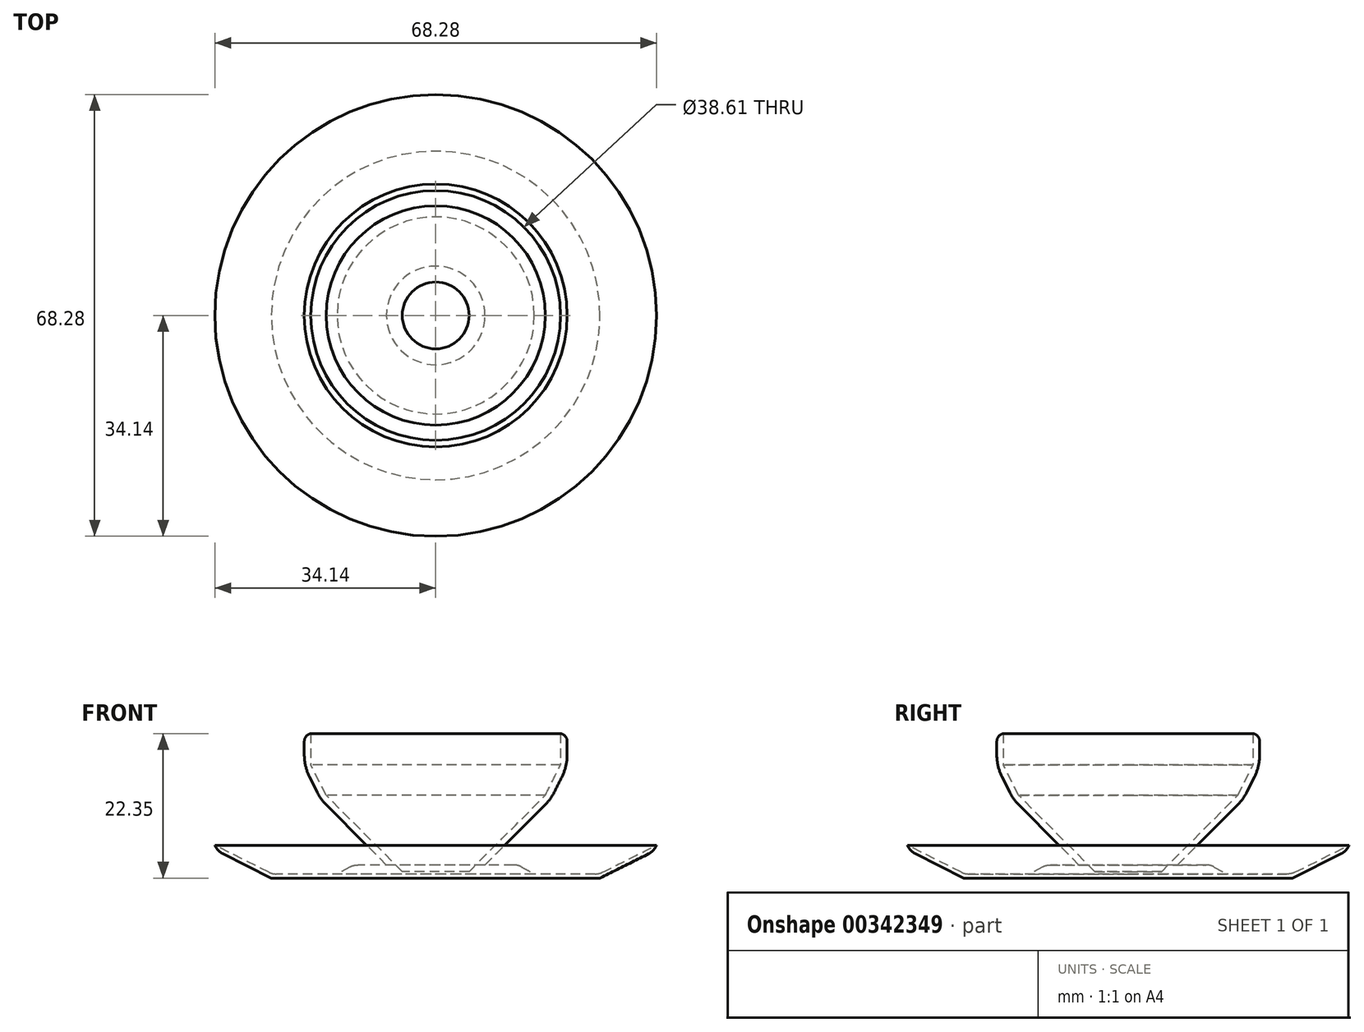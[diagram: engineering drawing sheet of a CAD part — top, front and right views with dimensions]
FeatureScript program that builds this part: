
annotation { "Feature Type Name" : "Feature", "Feature Type Description" : "" }
export const myFeature = defineFeature(function(context is Context, id is Id, definition is map)
    precondition{}
    {
        {
            var Q0;
            Q0=qCreatedBy(makeId("Top.planeOp"),FACE);
            var sketch = newSketch(context, id + "F0", { "sketchPlane" : qUnion([Q0])});
            skCircle(sketch, "E0", {"center": v(0, 0) * mm, "radius": 25.4 * mm});
            skSolve(sketch);
        }
        {
            var Q0;
            Q0=qCreatedBy(makeId("Top.planeOp"),FACE);
            cPlane(context, id + "F1", {"entities" : qUnion([Q0]), "cplaneType" : CPlaneType.OFFSET, "offset" : 5.08 * mm, "width" : 152.4 * mm, "height" : 152.4 * mm});
        }
        {
            var Q0;
            Q0=qCreatedBy(id+"F1.planeOp",FACE);
            var sketch = newSketch(context, id + "F2", { "sketchPlane" : qUnion([Q0])});
            skCircle(sketch, "E1", {"center": v(0, 0) * mm, "radius": 35.56 * mm});
            skSolve(sketch);
        }
        {
            var Q0;
            Q0 = qSketchRegion(id + "F0", true);
            var Q1;
            Q1=makeQuery(id+"F2.imprint","IMPRINT",FACE,{"disambiguationData":[TD([[makeQuery(id+"F2.imprint","IMPRINT",EDGE,{"derivedFrom":sQuery(id+"F2.wireOp",EDGE,"E1")}),1.0]])]});
            loft(context, id + "F3", {"sheetProfilesArray" : [{ "sheetProfileEntities" : qUnion([Q0]) }, { "sheetProfileEntities" : qUnion([Q1]) }]});
        }
        {
            var Q0;
            Q0=makeQuery(id+"F3.opLoft","CAP_FACE",FACE,{"disambiguationData":[OSD([makeQuery(id+"F2.imprint","IMPRINT",FACE,{"disambiguationData":[TD([[makeQuery(id+"F2.imprint","IMPRINT",EDGE,{"derivedFrom":sQuery(id+"F2.wireOp",EDGE,"E1")}),1.0]])]})])],"isStart":true});
            shell(context, id + "F4", {"entities" : qUnion([Q0]), "thickness" : 0.64 * mm});
        }
        {
            var Q0;
            Q0=qCreatedBy(makeId("Top.planeOp"),FACE);
            var Q1;
            Q1 = qBodyType(qCreatedBy(id + "FbNprcCNBa9596W_1" ,EDGE), BodyType.WIRE);
            cPlane(context, id + "F5", {"entities" : qUnion([Q0, Q1]), "cplaneType" : CPlaneType.OFFSET, "offset" : 2.03 * mm, "width" : 152.4 * mm, "height" : 152.4 * mm});
        }
        {
            var Q0;
            Q0=qCreatedBy(id+"F5.planeOp",FACE);
            var sketch = newSketch(context, id + "F6", { "sketchPlane" : qUnion([Q0])});
            skCircle(sketch, "E2", {"center": v(0, 0) * mm, "radius": 12.7 * mm});
            skSolve(sketch);
        }
        {
            var Q0;
            Q0=makeQuery(id+"F4.opShell","OFFSET_FACE",FACE,{"disambiguationData":[OSD([makeQuery(id+"F0.imprint","IMPRINT",FACE,{"disambiguationData":[TD([[makeQuery(id+"F0.imprint","IMPRINT",EDGE,{"derivedFrom":sQuery(id+"F0.wireOp",EDGE,"E0")}),1.0]])]})])]});
            var sketch = newSketch(context, id + "F7", { "sketchPlane" : qUnion([Q0])});
            skCircle(sketch, "E3", {"center": v(0, 0) * mm, "radius": 15.24 * mm});
            skSolve(sketch);
        }
        {
            var Q1;
            Q1=makeQuery(id+"F7.imprint","IMPRINT",FACE,{"disambiguationData":[TD([[makeQuery(id+"F7.imprint","IMPRINT",EDGE,{"derivedFrom":sQuery(id+"F7.wireOp",EDGE,"E3")}),1.0]])]});
            var Q2;
            Q2=makeQuery(id+"F6.imprint","IMPRINT",FACE,{"disambiguationData":[TD([[makeQuery(id+"F6.imprint","IMPRINT",EDGE,{"derivedFrom":sQuery(id+"F6.wireOp",EDGE,"E2")}),1.0]])]});
            loft(context, id + "F8", {"operationType" : NewBodyOperationType.ADD, "sheetProfilesArray" : [{ "sheetProfileEntities" : qUnion([Q1]) }, { "sheetProfileEntities" : qUnion([Q2]) }]});
        }
        {
            var Q0;
            Q0=makeQuery(id+"F6.imprint","IMPRINT",FACE,{"disambiguationData":[TD([[makeQuery(id+"F6.imprint","IMPRINT",EDGE,{"derivedFrom":sQuery(id+"F6.wireOp",EDGE,"E2")}),1.0]])]});
            var sketch = newSketch(context, id + "F9", { "sketchPlane" : qUnion([Q0])});
            skCircle(sketch, "E4", {"center": v(0, 0) * mm, "radius": 7.62 * mm});
            skSolve(sketch);
        }
        {
            var Q0;
            Q0=qCreatedBy(id+"F5.planeOp",FACE);
            cPlane(context, id + "F10", {"entities" : qUnion([Q0]), "cplaneType" : CPlaneType.OFFSET, "offset" : 5.08 * mm, "width" : 152.4 * mm, "height" : 152.4 * mm});
        }
        {
            var Q0;
            Q0=qCreatedBy(id+"F10.planeOp",FACE);
            var sketch = newSketch(context, id + "F11", { "sketchPlane" : qUnion([Q0])});
            skCircle(sketch, "E5", {"center": v(0, 0) * mm, "radius": 12.7 * mm});
            skSolve(sketch);
        }
        {
            var Q1;
            Q1=makeQuery(id+"F9.imprint","IMPRINT",FACE,{"disambiguationData":[TD([[makeQuery(id+"F9.imprint","IMPRINT",EDGE,{"derivedFrom":sQuery(id+"F9.wireOp",EDGE,"E4")}),1.0]])]});
            var Q2;
            Q2=makeQuery(id+"F11.imprint","IMPRINT",FACE,{"disambiguationData":[TD([[makeQuery(id+"F11.imprint","IMPRINT",EDGE,{"derivedFrom":sQuery(id+"F11.wireOp",EDGE,"E5")}),1.0]])]});
            loft(context, id + "F12", {"operationType" : NewBodyOperationType.ADD, "sheetProfilesArray" : [{ "sheetProfileEntities" : qUnion([Q1]) }, { "sheetProfileEntities" : qUnion([Q2]) }]});
        }
        {
            var Q0;
            Q0=qCreatedBy(id+"F10.planeOp",FACE);
            cPlane(context, id + "F13", {"entities" : qUnion([Q0]), "cplaneType" : CPlaneType.OFFSET, "offset" : 5.08 * mm, "width" : 152.4 * mm, "height" : 152.4 * mm});
        }
        {
            var Q0;
            Q0=qCreatedBy(id+"F13.planeOp",FACE);
            var sketch = newSketch(context, id + "F14", { "sketchPlane" : qUnion([Q0])});
            skCircle(sketch, "E6", {"center": v(0, 0) * mm, "radius": 17.78 * mm});
            skSolve(sketch);
        }
        {
            var Q1;
            Q1=makeQuery(id+"F12.opLoft","CAP_FACE",FACE,{"disambiguationData":[OSD([makeQuery(id+"F11.imprint","IMPRINT",FACE,{"disambiguationData":[TD([[makeQuery(id+"F11.imprint","IMPRINT",EDGE,{"derivedFrom":sQuery(id+"F11.wireOp",EDGE,"E5")}),1.0]])]})])],"isStart":true});
            var Q2;
            Q2=makeQuery(id+"F14.imprint","IMPRINT",FACE,{"disambiguationData":[TD([[makeQuery(id+"F14.imprint","IMPRINT",EDGE,{"derivedFrom":sQuery(id+"F14.wireOp",EDGE,"E6")}),1.0]])]});
            loft(context, id + "F15", {"operationType" : NewBodyOperationType.ADD, "sheetProfilesArray" : [{ "sheetProfileEntities" : qUnion([Q1]) }, { "sheetProfileEntities" : qUnion([Q2]) }]});
        }
        {
            var Q0;
            Q0=qCreatedBy(id+"F13.planeOp",FACE);
            cPlane(context, id + "F16", {"entities" : qUnion([Q0]), "cplaneType" : CPlaneType.OFFSET, "offset" : 5.08 * mm, "width" : 152.4 * mm, "height" : 152.4 * mm});
        }
        {
            var Q0;
            Q0=qCreatedBy(id+"F16.planeOp",FACE);
            var sketch = newSketch(context, id + "F17", { "sketchPlane" : qUnion([Q0])});
            skCircle(sketch, "E7", {"center": v(0, 0) * mm, "radius": 20.32 * mm});
            skSolve(sketch);
        }
        {
            var Q1;
            Q1=makeQuery(id+"F15.opLoft","CAP_FACE",FACE,{"disambiguationData":[OSD([makeQuery(id+"F14.imprint","IMPRINT",FACE,{"disambiguationData":[TD([[makeQuery(id+"F14.imprint","IMPRINT",EDGE,{"derivedFrom":sQuery(id+"F14.wireOp",EDGE,"E6")}),1.0]])]})])],"isStart":true});
            var Q2;
            Q2=makeQuery(id+"F17.imprint","IMPRINT",FACE,{"disambiguationData":[TD([[makeQuery(id+"F17.imprint","IMPRINT",EDGE,{"derivedFrom":sQuery(id+"F17.wireOp",EDGE,"E7")}),1.0]])]});
            loft(context, id + "F18", {"operationType" : NewBodyOperationType.ADD, "sheetProfilesArray" : [{ "sheetProfileEntities" : qUnion([Q1]) }, { "sheetProfileEntities" : qUnion([Q2]) }]});
        }
        {
            var Q0;
            Q0=makeQuery(id+"F18.opLoft","CAP_FACE",FACE,{"disambiguationData":[OSD([makeQuery(id+"F17.imprint","IMPRINT",FACE,{"disambiguationData":[TD([[makeQuery(id+"F17.imprint","IMPRINT",EDGE,{"derivedFrom":sQuery(id+"F17.wireOp",EDGE,"E7")}),1.0]])]})])],"isStart":true});
            extrude(context, id + "F19", {"entities" : qUnion([Q0]), "operationType" : NewBodyOperationType.ADD, "depth" : 5.08 * mm});
        }
        {
            var Q0;
            Q0=makeQuery(id+"F19.opExtrude","CAP_FACE",FACE,{"disambiguationData":[OSD([makeQuery(id+"F17.imprint","IMPRINT",FACE,{"disambiguationData":[TD([[makeQuery(id+"F17.imprint","IMPRINT",EDGE,{"derivedFrom":sQuery(id+"F17.wireOp",EDGE,"E7")}),1.0]])]})])],"isStart":false});
            shell(context, id + "F20", {"entities" : qUnion([Q0]), "thickness" : 1.02 * mm});
        }
        {
            var Q0;
            {var subQ0=sQuery(id+"F17.wireOp",EDGE,"E7");var subQ1=sQuery(id+"F14.wireOp",EDGE,"E6");var subQ2=sQuery(id+"F11.wireOp",EDGE,"E5");var subQ3=sQuery(id+"F9.wireOp",EDGE,"E4");Q0=makeQuery(id+"F19.boolean.opBoolean","MERGE",EDGE,{"derivedFrom":[makeQuery(id+"F18.opLoft","MID_CAP_EDGE",EDGE,{"disambiguationData":[OSD([subQ3,subQ2,subQ1,subQ0])],"capPos":1.0}),makeQuery(id+"F19.opExtrude","CAP_EDGE",EDGE,{"disambiguationData":[OSD([subQ3,subQ2,subQ1,subQ0])],"isStart":true})]});}
            fillet(context, id + "F21", {"entities" : qUnion([Q0]), "radius" : 7.62 * mm, "tangentPropagation" : true, "allowEdgeOverflow" : false});
        }
        {
            var Q0;
            {var subQ0=sQuery(id+"F14.wireOp",EDGE,"E6");var subQ1=sQuery(id+"F11.wireOp",EDGE,"E5");var subQ2=sQuery(id+"F9.wireOp",EDGE,"E4");Q0=makeQuery(id+"F18.boolean.opBoolean","MERGE",EDGE,{"derivedFrom":[makeQuery(id+"F15.opLoft","MID_CAP_EDGE",EDGE,{"disambiguationData":[OSD([subQ2,subQ1,subQ0])],"capPos":1.0}),makeQuery(id+"F18.opLoft","MID_CAP_EDGE",EDGE,{"disambiguationData":[OSD([subQ2,subQ1,subQ0])],"capPos":0.0})]});}
            fillet(context, id + "F22", {"entities" : qUnion([Q0]), "radius" : 7.62 * mm, "tangentPropagation" : true, "allowEdgeOverflow" : false});
        }
        {
            var Q0;
            Q0=makeQuery(id+"F19.opExtrude","CAP_EDGE",EDGE,{"disambiguationData":[OSD([sQuery(id+"F9.wireOp",EDGE,"E4"),sQuery(id+"F11.wireOp",EDGE,"E5"),sQuery(id+"F14.wireOp",EDGE,"E6"),sQuery(id+"F17.wireOp",EDGE,"E7")])],"isStart":false});
            fillet(context, id + "F23", {"entities" : qUnion([Q0]), "radius" : 1.27 * mm, "tangentPropagation" : true, "allowEdgeOverflow" : false});
        }
        {
            var Q0;
            Q0=makeQuery(id+"F3.opLoft","MID_CAP_EDGE",EDGE,{"disambiguationData":[OSD([sQuery(id+"F0.wireOp",EDGE,"E0"),sQuery(id+"F2.wireOp",EDGE,"E1")])],"capPos":1.0});
            fillet(context, id + "F24", {"entities" : qUnion([Q0]), "radius" : 2.54 * mm, "tangentPropagation" : true, "allowEdgeOverflow" : false});
        }
        {
            var Q0;
            Q0=makeQuery(id+"F4.opShell","OFFSET_EDGE",EDGE,{"disambiguationData":[OSD([sQuery(id+"F0.wireOp",EDGE,"E0")])]});
            fillet(context, id + "F25", {"entities" : qUnion([Q0]), "radius" : 2.54 * mm, "tangentPropagation" : true, "allowEdgeOverflow" : false});
        }
        {
            var Q0;
            Q0=makeQuery(id+"F8.opLoft","MID_CAP_EDGE",EDGE,{"disambiguationData":[OSD([sQuery(id+"F6.wireOp",EDGE,"E2"),sQuery(id+"F7.wireOp",EDGE,"E3")])],"capPos":1.0});
            fillet(context, id + "F26", {"entities" : qUnion([Q0]), "radius" : 2.54 * mm, "tangentPropagation" : true, "allowEdgeOverflow" : false});
        }
    });
